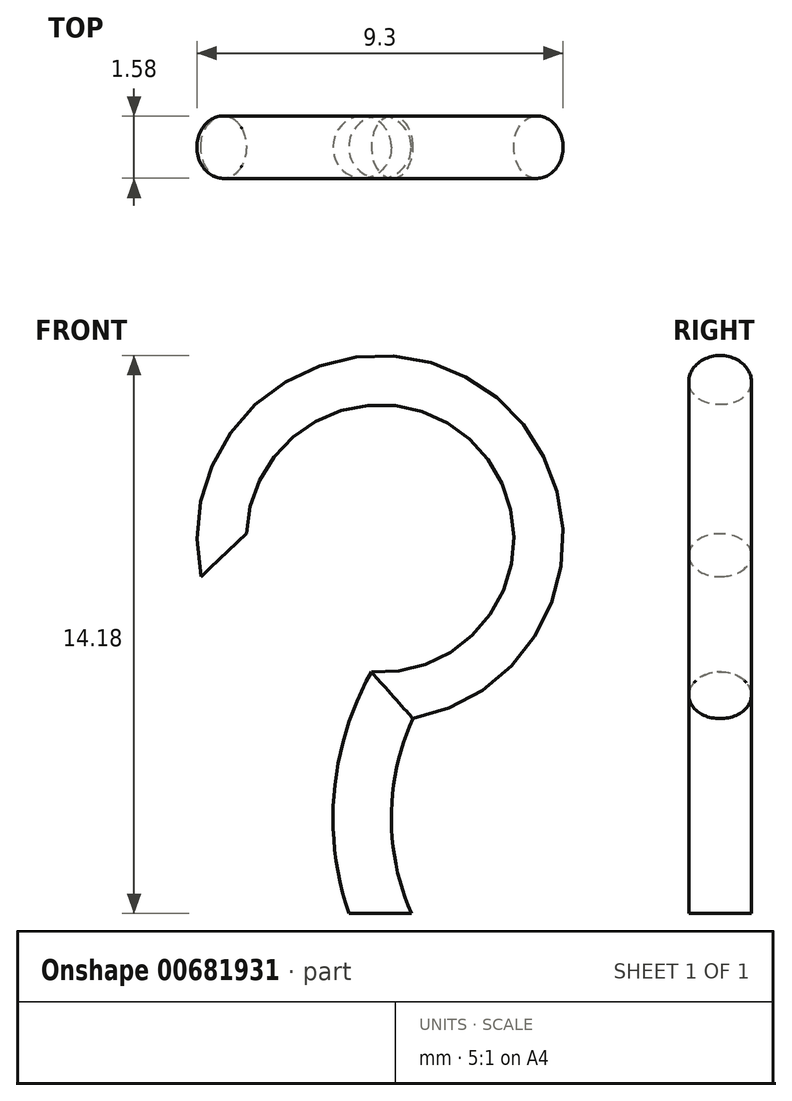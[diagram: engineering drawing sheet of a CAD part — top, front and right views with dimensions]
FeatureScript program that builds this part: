
annotation { "Feature Type Name" : "Feature", "Feature Type Description" : "" }
export const myFeature = defineFeature(function(context is Context, id is Id, definition is map)
    precondition{}
    {
        {
            var Q0;
            Q0=qCreatedBy(makeId("Front.planeOp"),FACE);
            var sketch = newSketch(context, id + "F0", { "sketchPlane" : qUnion([Q0])});
            skLineSegment(sketch, "E0", {"start": v(0, 0) * mm, "end": v(0, 2.43) * mm});
            skArc(sketch, "E1", {"start": v(2.12, 7.16) * mm, "mid": v(0.13, 12.7) * mm, "end": v(-2.3, 7.34) * mm});
            skLineSegment(sketch, "E2", {"start": v(0, 9.53) * mm, "end": v(-2.3, 7.34) * mm});
            skArc(sketch, "E3.filletArc", {"start": v(2.12, 7.16) * mm, "mid": v(0.55, 5.02) * mm, "end": v(0, 2.43) * mm});
            skSolve(sketch);
        }
        {
            var Q0;
            Q0=qCreatedBy(makeId("Top.planeOp"),FACE);
            var sketch = newSketch(context, id + "F1", { "sketchPlane" : qUnion([Q0])});
            skCircle(sketch, "E4", {"center": v(0, 0) * mm, "radius": 0.8 * mm});
            skSolve(sketch);
        }
        {
            var Q0;
            Q0=makeQuery(id+"F1.imprint","IMPRINT",FACE,{"disambiguationData":[TD([[makeQuery(id+"F1.imprint","IMPRINT",EDGE,{"derivedFrom":sQuery(id+"F1.wireOp",EDGE,"E4")}),1.0]])]});
            var Q1;
            Q1=sQuery(id+"F0.wireOp",EDGE,"E3.filletArc");
            var Q2;
            Q2=sQuery(id+"F0.wireOp",EDGE,"E1");
            sweep(context, id + "F2", {"profiles" : qUnion([Q0]), "path" : qUnion([Q1, Q2])});
        }
    });
